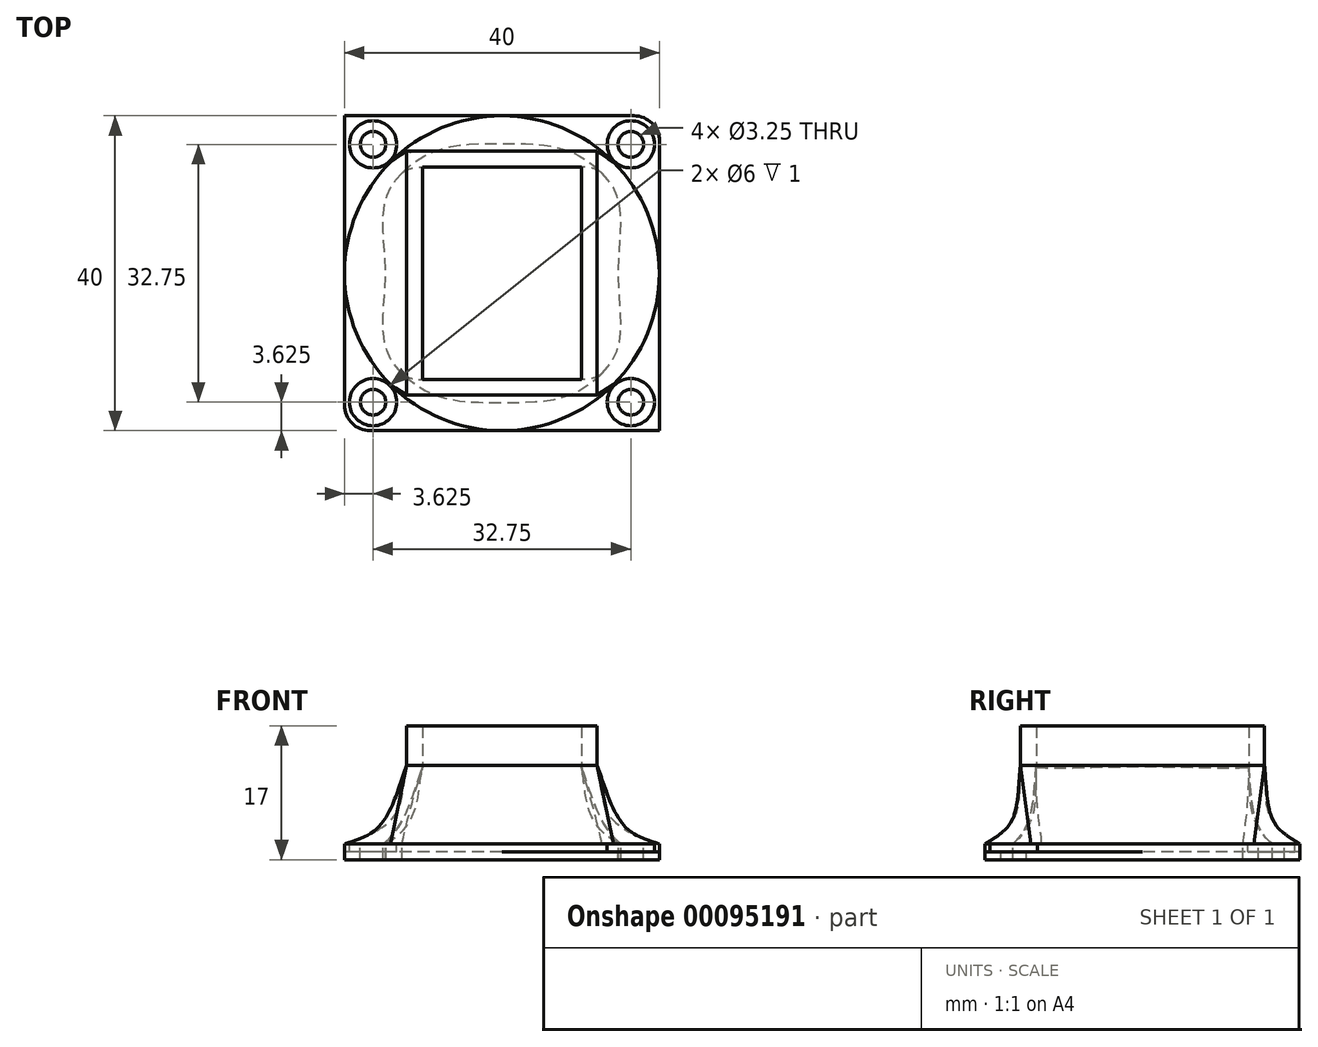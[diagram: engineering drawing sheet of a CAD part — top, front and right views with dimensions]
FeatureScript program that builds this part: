
annotation { "Feature Type Name" : "Feature", "Feature Type Description" : "" }
export const myFeature = defineFeature(function(context is Context, id is Id, definition is map)
    precondition{}
    {
        {
            assignVariable(context, id + "F0", {"name" : "ScrewID", "anyValue" : 3.25});
        }
        {
            assignVariable(context, id + "F1", {"name" : "WallThickness", "anyValue" : 2});
        }
        {
            var Q0;
            Q0=qCreatedBy(makeId("Top.planeOp"),FACE);
            var sketch = newSketch(context, id + "F2", { "sketchPlane" : qUnion([Q0])});
            skLineSegment(sketch, "E0", {"start": v(-20, -20) * mm, "end": v(20, -20) * mm});
            skLineSegment(sketch, "E1", {"start": v(20, -20) * mm, "end": v(20, 20) * mm});
            skLineSegment(sketch, "E2", {"start": v(20, 20) * mm, "end": v(-20, 20) * mm});
            skLineSegment(sketch, "E3", {"start": v(-20, 20) * mm, "end": v(-20, -20) * mm});
            skCircle(sketch, "E4", {"center": v(-16.37, -16.38) * mm, "radius": 1.63 * mm});
            skCircle(sketch, "E5", {"center": v(-16.37, -16.38) * mm, "radius": 3 * mm});
            skLineSegment(sketch, "E6", {"start": v(0, 20) * mm, "end": v(0, -20) * mm, "construction": true});
            skLineSegment(sketch, "E7", {"start": v(-20, 0) * mm, "end": v(20, 0) * mm, "construction": true});
            skCircle(sketch, "E8.MirrorC", {"center": v(16.38, -16.38) * mm, "radius": 3 * mm});
            skCircle(sketch, "E9.MirrorC", {"center": v(16.38, -16.38) * mm, "radius": 1.63 * mm});
            skCircle(sketch, "E10.MirrorC", {"center": v(16.38, 16.38) * mm, "radius": 1.63 * mm});
            skCircle(sketch, "E11.MirrorC", {"center": v(16.38, 16.38) * mm, "radius": 3 * mm});
            skCircle(sketch, "E12.MirrorC", {"center": v(-16.38, 16.38) * mm, "radius": 3 * mm});
            skCircle(sketch, "E13.MirrorC", {"center": v(-16.38, 16.38) * mm, "radius": 1.63 * mm});
            skCircle(sketch, "E14", {"center": v(0, 0) * mm, "radius": 18 * mm, "construction": true});
            skCircle(sketch, "E15", {"center": v(0, 0) * mm, "radius": 20 * mm});
            skSolve(sketch);
        }
        {
            assignVariable(context, id + "F3", {"name" : "MountThickness", "anyValue" : 2});
        }
        {
            assignVariable(context, id + "F4", {"name" : "ScrewHeadDepth", "anyValue" : getVariable(context, 'MountThickness') / 2});
        }
        {
            assignVariable(context, id + "F5", {"name" : "ChannelLength", "anyValue" : 10});
        }
        {
            assignVariable(context, id + "F6", {"name" : "BlowerOpeningDepth", "anyValue" : 5});
        }
        {
            var Q0;
            Q0=qCreatedBy(makeId("Top.planeOp"),FACE);
            cPlane(context, id + "F7", {"entities" : qUnion([Q0]), "cplaneType" : CPlaneType.OFFSET, "offset" : (getVariable(context, 'ChannelLength')) * mm, "width" : 150 * mm, "height" : 150 * mm});
        }
        {
            var Q0;
            Q0=qCreatedBy(id+"F7.planeOp",FACE);
            var sketch = newSketch(context, id + "F8", { "sketchPlane" : qUnion([Q0])});
            skLineSegment(sketch, "E16", {"start": v(-12.1, 15.5) * mm, "end": v(-12.1, -15.5) * mm});
            skLineSegment(sketch, "E17", {"start": v(-12.1, -15.5) * mm, "end": v(12.1, -15.5) * mm});
            skLineSegment(sketch, "E18", {"start": v(12.1, -15.5) * mm, "end": v(12.1, 15.5) * mm});
            skLineSegment(sketch, "E19", {"start": v(12.1, 15.5) * mm, "end": v(-12.1, 15.5) * mm});
            skLineSegment(sketch, "E20.0", {"start": v(-20, 20) * mm, "end": v(-20, -20) * mm, "construction": true});
            skLineSegment(sketch, "E20.1", {"start": v(-20, -20) * mm, "end": v(20, -20) * mm, "construction": true});
            skLineSegment(sketch, "E20.2", {"start": v(20, -20) * mm, "end": v(20, 20) * mm, "construction": true});
            skLineSegment(sketch, "E20.3", {"start": v(20, 20) * mm, "end": v(-20, 20) * mm, "construction": true});
            skPoint(sketch, "E21", {"position": v(0, 0) * mm});
            skSolve(sketch);
        }
        {
            var Q0;
            Q0=qCreatedBy(makeId("Front.planeOp"),FACE);
            var sketch = newSketch(context, id + "F9", { "sketchPlane" : qUnion([Q0])});
            skFitSpline(sketch, "E22", {"points": [v(-12.1, 10) * mm, v(-20, 0) * mm], "startDerivative": vector(-2.58, -15.43) * mm, "endDerivative": vector(-23.87, -7.5) * mm});
            skLineSegment(sketch, "E23.0", {"start": v(12.1, 10) * mm, "end": v(-12.1, 10) * mm, "construction": true});
            skLineSegment(sketch, "E24", {"start": v(0, 10) * mm, "end": v(0, 0) * mm, "construction": true});
            skFitSpline(sketch, "E25.MirrorCS", {"points": [v(12.1, 10) * mm, v(20, 0) * mm], "startDerivative": vector(2.58, -15.43) * mm, "endDerivative": vector(23.87, -7.5) * mm});
            skSolve(sketch);
        }
        {
            var Q0;
            Q0=qCreatedBy(makeId("Right.planeOp"),FACE);
            var sketch = newSketch(context, id + "F10", { "sketchPlane" : qUnion([Q0])});
            skFitSpline(sketch, "E26", {"points": [v(-15.5, 10) * mm, v(-20, 0) * mm], "startDerivative": vector(-0.99, -14.83) * mm, "endDerivative": vector(-16.14, -9.43) * mm});
            skLineSegment(sketch, "E27.0", {"start": v(-15.5, 10) * mm, "end": v(15.5, 10) * mm, "construction": true});
            skLineSegment(sketch, "E28", {"start": v(0, 10) * mm, "end": v(0, 0) * mm, "construction": true});
            skFitSpline(sketch, "E29.MirrorCS", {"points": [v(15.5, 10) * mm, v(20, 0) * mm], "startDerivative": vector(0.99, -14.83) * mm, "endDerivative": vector(16.14, -9.43) * mm});
            skSolve(sketch);
        }
        {
            var Q0;
            Q0=makeQuery(id+"F8.imprint","IMPRINT",FACE,{"disambiguationData":[TD([[makeQuery(id+"F8.imprint","IMPRINT",EDGE,{"derivedFrom":sQuery(id+"F8.wireOp",EDGE,"E16")}),1.0]])]});
            var Q1;
            {var subQ0=sQuery(id+"F2.wireOp",EDGE,"E15");var subQ1=makeQuery(id+"F2.imprint","INTERSECT",VERTEX,{"derivedFrom":[sQuery(id+"F2.wireOp",EDGE,"E1"),subQ0]});Q1=makeQuery(id+"F2.imprint","IMPRINT",FACE,{"disambiguationData":[TD([[makeQuery(id+"F2.imprint","IMPRINT",EDGE,{"disambiguationData":[TD([[subQ1,-1.0]])],"derivedFrom":subQ0}),1.0]])]});}
            var Q2;
            Q2=sQuery(id+"F10.wireOp",EDGE,"E26");
            var Q3;
            Q3=sQuery(id+"F9.wireOp",EDGE,"E25.MirrorCS");
            var Q4;
            Q4=sQuery(id+"F10.wireOp",EDGE,"E29.MirrorCS");
            var Q5;
            Q5=sQuery(id+"F9.wireOp",EDGE,"E22");
            loft(context, id + "F11", {"addGuides" : true, "sheetProfilesArray" : [{ "sheetProfileEntities" : qUnion([Q0]) }, { "sheetProfileEntities" : qUnion([Q1]) }], "guidesArray" : [{ "guideEntities" : qUnion([Q2]), "guideDerivativeType" : LoftGuideDerivativeType.DEFAULT, "guideDerivativeMagnitude" : 1 }, { "guideEntities" : qUnion([Q3]), "guideDerivativeType" : LoftGuideDerivativeType.DEFAULT, "guideDerivativeMagnitude" : 1 }, { "guideEntities" : qUnion([Q4]), "guideDerivativeType" : LoftGuideDerivativeType.DEFAULT, "guideDerivativeMagnitude" : 1 }, { "guideEntities" : qUnion([Q5]), "guideDerivativeType" : LoftGuideDerivativeType.DEFAULT, "guideDerivativeMagnitude" : 1 }]});
        }
        {
            var Q0;
            Q0=makeQuery(id+"F2.imprint","IMPRINT",FACE,{"disambiguationData":[TD([[makeQuery(id+"F2.imprint","IMPRINT",EDGE,{"derivedFrom":sQuery(id+"F2.wireOp",EDGE,"E14")}),-1.0]])]});
            var Q1;
            {var subQ0=sQuery(id+"F2.wireOp",EDGE,"E12.MirrorC");Q1=makeQuery(id+"F2.imprint","IMPRINT",FACE,{"disambiguationData":[TD([[makeQuery(id+"F2.imprint","IMPRINT",EDGE,{"derivedFrom":subQ0}),1.0]])]});}
            var Q2;
            {var subQ0=sQuery(id+"F2.wireOp",EDGE,"E11.MirrorC");Q2=makeQuery(id+"F2.imprint","IMPRINT",FACE,{"disambiguationData":[TD([[makeQuery(id+"F2.imprint","IMPRINT",EDGE,{"derivedFrom":subQ0}),-1.0]])]});}
            var Q3;
            {var subQ3=sQuery(id+"F2.wireOp",EDGE,"E8.MirrorC");Q3=makeQuery(id+"F2.imprint","IMPRINT",FACE,{"disambiguationData":[TD([[makeQuery(id+"F2.imprint","IMPRINT",EDGE,{"derivedFrom":subQ3}),1.0]])]});}
            var Q4;
            {var subQ3=sQuery(id+"F2.wireOp",EDGE,"E5");Q4=makeQuery(id+"F2.imprint","IMPRINT",FACE,{"disambiguationData":[TD([[makeQuery(id+"F2.imprint","IMPRINT",EDGE,{"derivedFrom":subQ3}),-1.0]])]});}
            var Q5;
            {var subQ0=sQuery(id+"F2.wireOp",EDGE,"E15");var subQ1=makeQuery(id+"F2.imprint","INTERSECT",VERTEX,{"derivedFrom":[sQuery(id+"F2.wireOp",EDGE,"E1"),subQ0]});Q5=makeQuery(id+"F2.imprint","IMPRINT",FACE,{"disambiguationData":[TD([[makeQuery(id+"F2.imprint","IMPRINT",EDGE,{"disambiguationData":[TD([[subQ1,-1.0]])],"derivedFrom":subQ0}),1.0]])]});}
            extrude(context, id + "F12", {"entities" : qUnion([Q0, Q1, Q2, Q3, Q4, Q5]), "operationType" : NewBodyOperationType.ADD, "oppositeDirection" : true, "depth" : (getVariable(context, 'MountThickness')) * mm});
        }
        {
            var Q0;
            Q0=makeQuery(id+"F2.imprint","IMPRINT",FACE,{"disambiguationData":[TD([[makeQuery(id+"F2.imprint","IMPRINT",EDGE,{"derivedFrom":sQuery(id+"F2.wireOp",EDGE,"E12.MirrorC")}),-1.0]])]});
            var Q1;
            Q1=makeQuery(id+"F2.imprint","IMPRINT",FACE,{"disambiguationData":[TD([[makeQuery(id+"F2.imprint","IMPRINT",EDGE,{"derivedFrom":sQuery(id+"F2.wireOp",EDGE,"E10.MirrorC")}),-1.0]])]});
            var Q2;
            Q2=makeQuery(id+"F2.imprint","IMPRINT",FACE,{"disambiguationData":[TD([[makeQuery(id+"F2.imprint","IMPRINT",EDGE,{"derivedFrom":sQuery(id+"F2.wireOp",EDGE,"E8.MirrorC")}),-1.0]])]});
            var Q3;
            Q3=makeQuery(id+"F2.imprint","IMPRINT",FACE,{"disambiguationData":[TD([[makeQuery(id+"F2.imprint","IMPRINT",EDGE,{"derivedFrom":sQuery(id+"F2.wireOp",EDGE,"E4")}),-1.0]])]});
            extrude(context, id + "F13", {"entities" : qUnion([Q0, Q1, Q2, Q3]), "operationType" : NewBodyOperationType.ADD, "oppositeDirection" : true, "depth" : (getVariable(context, 'MountThickness')) * mm, "hasSecondDirection" : true, "secondDirectionOppositeDirection" : true, "secondDirectionDepth" : (getVariable(context, 'ScrewHeadDepth')) * mm});
        }
        {
            var Q0;
            Q0=makeQuery(id+"F11.opLoft","CAP_FACE",FACE,{"disambiguationData":[OSD([makeQuery(id+"F8.imprint","IMPRINT",FACE,{"disambiguationData":[TD([[makeQuery(id+"F8.imprint","IMPRINT",EDGE,{"derivedFrom":sQuery(id+"F8.wireOp",EDGE,"E16")}),1.0]])]})])],"isStart":true});
            extrude(context, id + "F14", {"entities" : qUnion([Q0]), "operationType" : NewBodyOperationType.ADD, "depth" : (getVariable(context, 'BlowerOpeningDepth')) * mm});
        }
        {
            var Q0;
            Q0=makeQuery(id+"F14.opExtrude","CAP_FACE",FACE,{"disambiguationData":[OSD([makeQuery(id+"F8.imprint","IMPRINT",FACE,{"disambiguationData":[TD([[makeQuery(id+"F8.imprint","IMPRINT",EDGE,{"derivedFrom":sQuery(id+"F8.wireOp",EDGE,"E16")}),1.0]])]})])],"isStart":false});
            var Q1;
            {var subQ0=sQuery(id+"F2.wireOp",EDGE,"E15");var subQ1=makeQuery(id+"F2.imprint","INTERSECT",VERTEX,{"derivedFrom":[sQuery(id+"F2.wireOp",EDGE,"E1"),subQ0]});Q1=makeQuery(id+"F11.opLoft","SWEPT_BODY",BODY,{"disambiguationData":[OSD([makeQuery(id+"F2.imprint","IMPRINT",FACE,{"disambiguationData":[TD([[makeQuery(id+"F2.imprint","IMPRINT",EDGE,{"disambiguationData":[TD([[subQ1,-1.0]])],"derivedFrom":subQ0}),1.0]])]}),makeQuery(id+"F8.imprint","IMPRINT",FACE,{"disambiguationData":[TD([[makeQuery(id+"F8.imprint","IMPRINT",EDGE,{"derivedFrom":sQuery(id+"F8.wireOp",EDGE,"E16")}),1.0]])]}),sQuery(id+"F9.wireOp",EDGE,"E22"),sQuery(id+"F9.wireOp",EDGE,"E25.MirrorCS"),sQuery(id+"F10.wireOp",EDGE,"E26"),sQuery(id+"F10.wireOp",EDGE,"E29.MirrorCS")])]});}
            shell(context, id + "F15", {"entities" : qUnion([Q0]), "parts" : qUnion([Q1]), "thickness" : (getVariable(context, 'WallThickness')) * mm});
        }
        {
            var Q0;
            Q0=makeQuery(id+"F15.opShell","OFFSET_FACE",FACE,{"disambiguationData":[OSD([sQuery(id+"F2.wireOp",EDGE,"E0"),sQuery(id+"F2.wireOp",EDGE,"E1"),sQuery(id+"F2.wireOp",EDGE,"E2"),sQuery(id+"F2.wireOp",EDGE,"E3"),sQuery(id+"F2.wireOp",EDGE,"E4"),sQuery(id+"F2.wireOp",EDGE,"E5"),sQuery(id+"F2.wireOp",EDGE,"E8.MirrorC"),sQuery(id+"F2.wireOp",EDGE,"E9.MirrorC"),sQuery(id+"F2.wireOp",EDGE,"E10.MirrorC"),sQuery(id+"F2.wireOp",EDGE,"E11.MirrorC"),sQuery(id+"F2.wireOp",EDGE,"E12.MirrorC"),sQuery(id+"F2.wireOp",EDGE,"E13.MirrorC")])]});
            extrude(context, id + "F16", {"entities" : qUnion([Q0]), "operationType" : NewBodyOperationType.REMOVE, "endBound" : BoundingType.THROUGH_ALL, "oppositeDirection" : true, "depth" : 25 * mm});
        }
        {
            var Q0;
            Q0=makeQuery(id+"F12.opExtrude","SWEPT_EDGE",EDGE,{"disambiguationData":[OSD([sQuery(id+"F2.wireOp",EDGE,"E0"),sQuery(id+"F2.wireOp",EDGE,"E1")])]});
            var Q1;
            Q1=makeQuery(id+"F12.opExtrude","SWEPT_EDGE",EDGE,{"disambiguationData":[OSD([sQuery(id+"F2.wireOp",EDGE,"E2"),sQuery(id+"F2.wireOp",EDGE,"E3")])]});
            var Q2;
            Q2=makeQuery(id+"F12.opExtrude","SWEPT_EDGE",EDGE,{"disambiguationData":[OSD([sQuery(id+"F2.wireOp",EDGE,"E1"),sQuery(id+"F2.wireOp",EDGE,"E2")])]});
            var Q3;
            Q3=makeQuery(id+"F12.opExtrude","SWEPT_EDGE",EDGE,{"disambiguationData":[OSD([sQuery(id+"F2.wireOp",EDGE,"E0"),sQuery(id+"F2.wireOp",EDGE,"E3")])]});
            fillet(context, id + "F17", {"entities" : qUnion([Q0, Q1, Q2, Q3]), "radius" : (getVariable(context, 'ScrewID')) * mm, "tangentPropagation" : true, "allowEdgeOverflow" : false});
        }
    });
